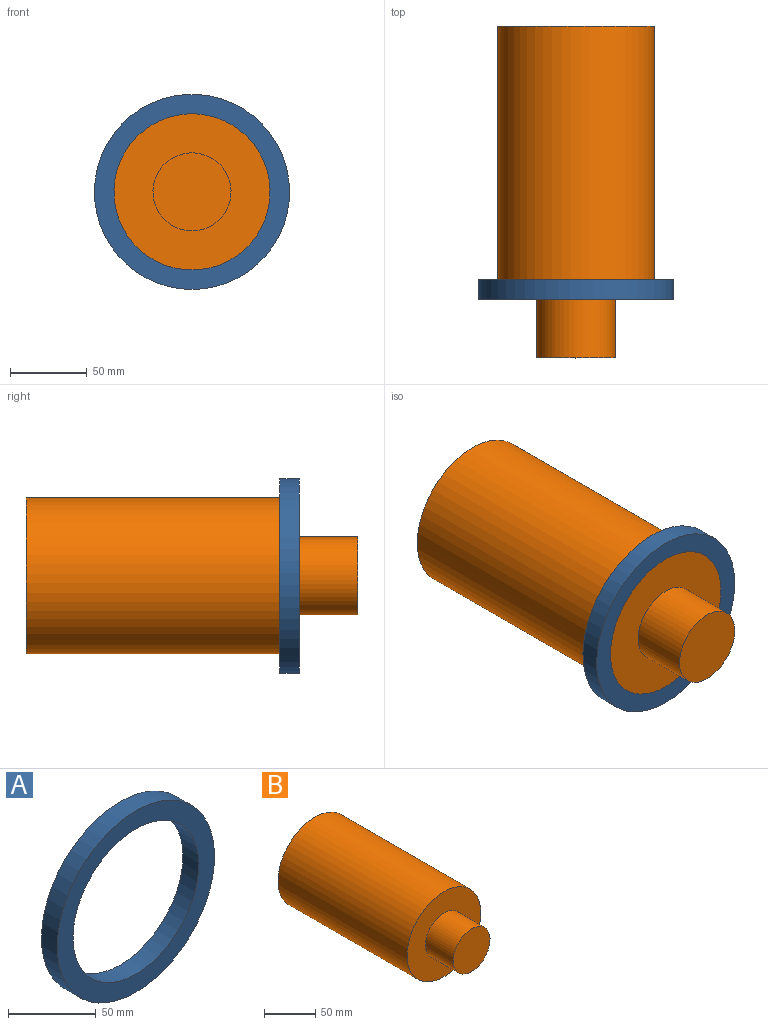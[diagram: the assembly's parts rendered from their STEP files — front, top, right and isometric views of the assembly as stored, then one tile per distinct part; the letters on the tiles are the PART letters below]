
ASSEMBLY  parts=2 mates=1
PART A: 4 faces, bbox 127x12.7x127 mm
  f0: cylinder r=50.8mm len=101.6mm, axis (0,1,0), area 4053.7mm2, adj f2,f3
  f1: cylinder r=63.5mm len=127mm, axis (0,1,0), area 5067.1mm2, adj f2,f3
  f2: plane 127x127mm, normal (0,-1,0), area 4560.4mm2, adj f0,f1
  f3: plane 127x127mm, normal (0,1,0), area 4560.4mm2, adj f0,f1
PART B: 5 faces, bbox 101.6x215.9x101.6 mm
  f0: cylinder r=50.8mm len=177.8mm, axis (0,1,0), area 56751.2mm2, adj f1,f2
  f1: plane 101.6x101.6mm, normal (0,-1,0), area 6080.5mm2, adj f0,f3
  f2: plane 101.6x101.6mm, normal (0,1,0), area 8107.3mm2, adj f0
  f3: cylinder r=25.4mm len=50.8mm, axis (0,1,0), area 6080.5mm2, adj f1,f4
  f4: plane 50.8x50.8mm, normal (0,-1,0), area 2026.8mm2, adj f3
PLACE A t=(73.22,-12.34,-44.78)mm
PLACE B t=(73.22,152.76,-44.78)mm
MATE slider A.f1 <-> B.f0  axis (0,-1,0) through (73.22,-25.04,-44.78)mm
